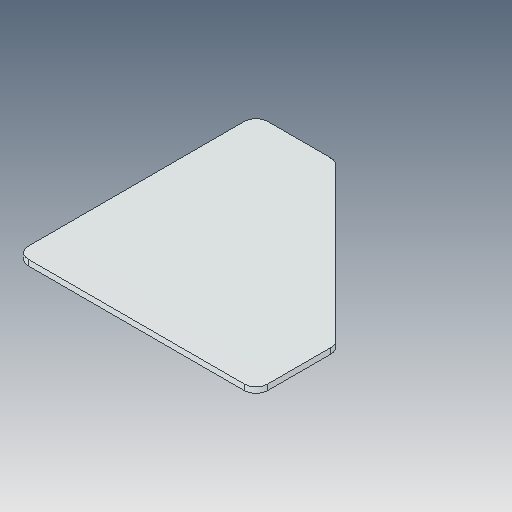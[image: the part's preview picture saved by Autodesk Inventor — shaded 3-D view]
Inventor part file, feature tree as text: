
AUTODESK INVENTOR PART (.ipt)
format: ipt  version: 2023.5 (Build 275446000, 446)  size: 85,504 bytes
history: native  units: in
note: dims shown in document units (in); Inventor stores cm internally (conversion verified against a paired STEP export)
features: fillet x1
ambient origin geometry x8: Origin, YZ Plane, XZ Plane, XY Plane, X Axis, Y Axis, Z Axis, Center Point
bodies: Solid1 (feature_tree)
feature tree (1):
  fillet  "Fillet1"  [1 undecoded]
note: 1 required parameter value undecoded (feature->parameter linkage not recoverable at this tier; creation-order binding heuristic only, values carry confidence <= 0.55)
